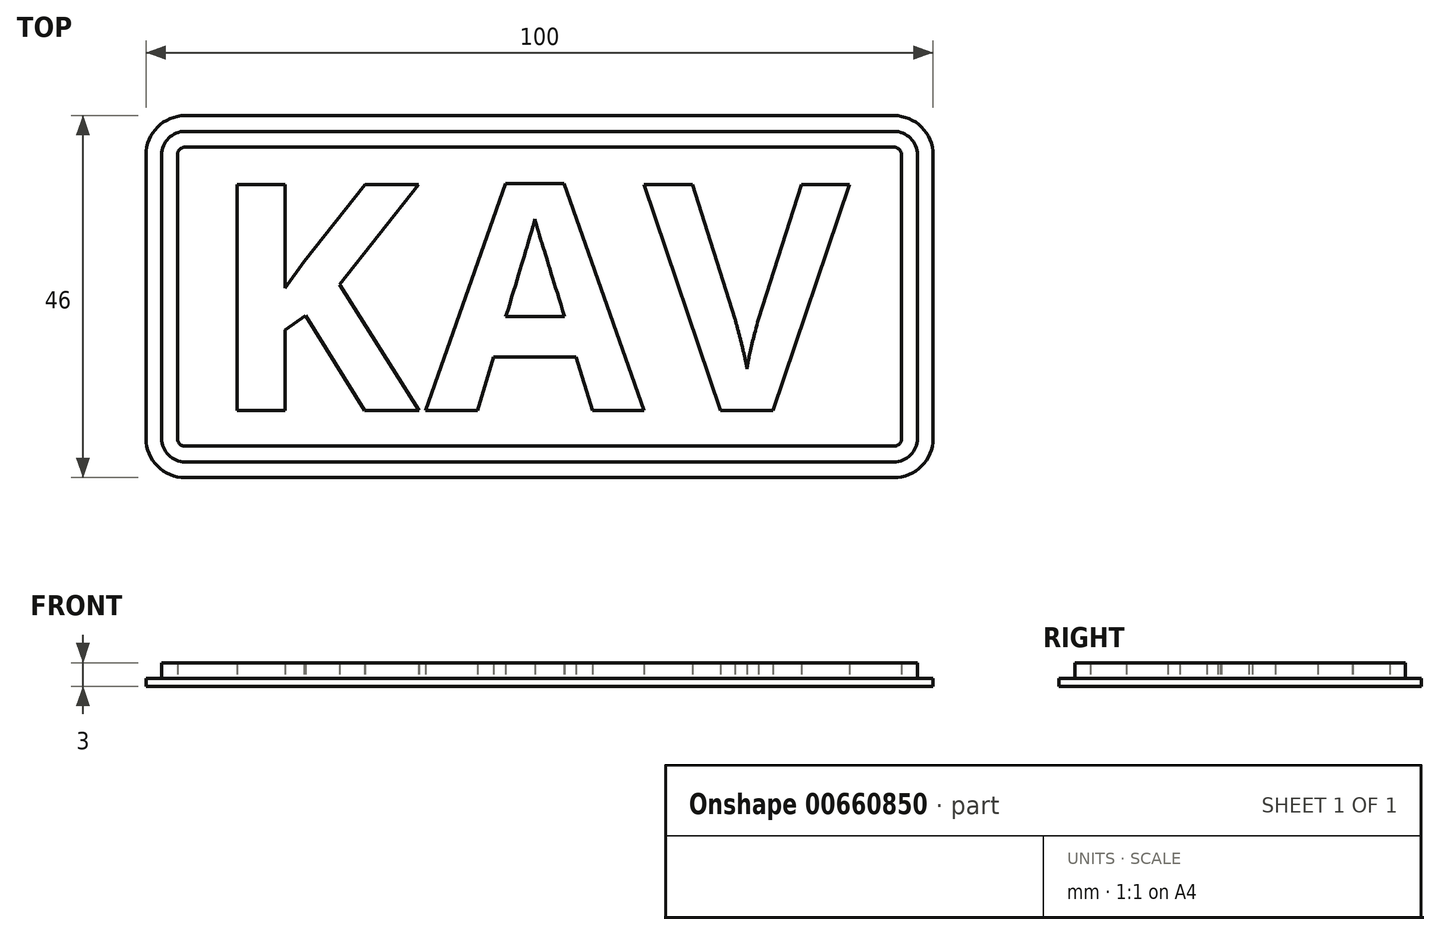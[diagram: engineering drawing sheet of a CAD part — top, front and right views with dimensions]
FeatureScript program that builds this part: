
annotation { "Feature Type Name" : "Feature", "Feature Type Description" : "" }
export const myFeature = defineFeature(function(context is Context, id is Id, definition is map)
    precondition{}
    {
        {
            assignVariable(context, id + "F0", {"variableType" : VariableType.LENGTH, "name" : "st", "lengthValue" : 1 * mm});
        }
        {
            assignVariable(context, id + "F1", {"variableType" : VariableType.LENGTH, "name" : "ft", "lengthValue" : 2 * mm});
        }
        {
            var Q0;
            Q0=qCreatedBy(makeId("Top.planeOp"),FACE);
            var sketch = newSketch(context, id + "F2", { "sketchPlane" : qUnion([Q0])});
            skLineSegment(sketch, "E0.bottom", {"start": v(-45, 23) * mm, "end": v(45, 23) * mm});
            skLineSegment(sketch, "E0.top", {"start": v(-45, -23) * mm, "end": v(45, -23) * mm});
            skLineSegment(sketch, "E0.left", {"start": v(-50, 18) * mm, "end": v(-50, -18) * mm});
            skLineSegment(sketch, "E0.right", {"start": v(50, 18) * mm, "end": v(50, -18) * mm});
            skPoint(sketch, "E1", {"position": v(0, 23) * mm});
            skPoint(sketch, "E2", {"position": v(-50, 0) * mm});
            skPoint(sketch, "E3.visualSharp", {"position": v(-50, 23) * mm});
            skArc(sketch, "E3.filletArc", {"start": v(-45, 23) * mm, "mid": v(-48.54, 21.54) * mm, "end": v(-50, 18) * mm});
            skPoint(sketch, "E4.visualSharp", {"position": v(50, 23) * mm});
            skArc(sketch, "E4.filletArc", {"start": v(50, 18) * mm, "mid": v(48.54, 21.54) * mm, "end": v(45, 23) * mm});
            skPoint(sketch, "E5.visualSharp", {"position": v(50, -23) * mm});
            skArc(sketch, "E5.filletArc", {"start": v(45, -23) * mm, "mid": v(48.54, -21.54) * mm, "end": v(50, -18) * mm});
            skPoint(sketch, "E6.visualSharp", {"position": v(-50, -23) * mm});
            skArc(sketch, "E6.filletArc", {"start": v(-50, -18) * mm, "mid": v(-48.54, -21.54) * mm, "end": v(-45, -23) * mm});
            skSolve(sketch);
        }
        {
            var Q0;
            Q0=qSketchRegion(id+"F2",true);
            extrude(context, id + "F3", {"entities" : qUnion([Q0]), "depth" : getVariable(context, 'st'), "offsetDistance" : 25 * mm});
        }
        {
            var Q0;
            Q0=makeQuery(id+"F3.opExtrude","CAP_FACE",FACE,{"disambiguationData":[OSD([sQuery(id+"F2.wireOp",EDGE,"E0.bottom"),sQuery(id+"F2.wireOp",EDGE,"E0.top"),sQuery(id+"F2.wireOp",EDGE,"E0.left"),sQuery(id+"F2.wireOp",EDGE,"E0.right"),sQuery(id+"F2.wireOp",EDGE,"E3.filletArc"),sQuery(id+"F2.wireOp",EDGE,"E4.filletArc"),sQuery(id+"F2.wireOp",EDGE,"E5.filletArc"),sQuery(id+"F2.wireOp",EDGE,"E6.filletArc")])],"isStart":false});
            var sketch = newSketch(context, id + "F4", { "sketchPlane" : qUnion([Q0])});
            skArc(sketch, "E7.0", {"start": v(-45, 21) * mm, "mid": v(-47.12, 20.12) * mm, "end": v(-48, 18) * mm});
            skLineSegment(sketch, "E7.1", {"start": v(-45, 21) * mm, "end": v(45, 21) * mm});
            skLineSegment(sketch, "E7.2", {"start": v(-48, 18) * mm, "end": v(-48, -18) * mm});
            skArc(sketch, "E7.3", {"start": v(48, 18) * mm, "mid": v(47.12, 20.12) * mm, "end": v(45, 21) * mm});
            skArc(sketch, "E7.4", {"start": v(-48, -18) * mm, "mid": v(-47.12, -20.12) * mm, "end": v(-45, -21) * mm});
            skLineSegment(sketch, "E7.5", {"start": v(-45, -21) * mm, "end": v(45, -21) * mm});
            skArc(sketch, "E7.6", {"start": v(45, -21) * mm, "mid": v(47.12, -20.12) * mm, "end": v(48, -18) * mm});
            skLineSegment(sketch, "E7.7", {"start": v(48, 18) * mm, "end": v(48, -18) * mm});
            skArc(sketch, "E8.0", {"start": v(-45, 19) * mm, "mid": v(-45.7, 18.7) * mm, "end": v(-46, 18) * mm});
            skLineSegment(sketch, "E8.1", {"start": v(-45, 19) * mm, "end": v(45, 19) * mm});
            skLineSegment(sketch, "E8.2", {"start": v(-46, 18) * mm, "end": v(-46, -18) * mm});
            skArc(sketch, "E8.3", {"start": v(46, 18) * mm, "mid": v(45.7, 18.7) * mm, "end": v(45, 19) * mm});
            skArc(sketch, "E8.4", {"start": v(-46, -18) * mm, "mid": v(-45.7, -18.7) * mm, "end": v(-45, -19) * mm});
            skLineSegment(sketch, "E8.5", {"start": v(-45, -19) * mm, "end": v(45, -19) * mm});
            skArc(sketch, "E8.6", {"start": v(45, -19) * mm, "mid": v(45.7, -18.7) * mm, "end": v(46, -18) * mm});
            skLineSegment(sketch, "E8.7", {"start": v(46, 18) * mm, "end": v(46, -18) * mm});
            skText(sketch, "E9", { "text": "KAV", "fontName": "OpenSans-Bold.ttf"});
            const initialGuessF4  = {"E9": [-0.042, -0.01447, 1, 0, 0.02894]};
            skSetInitialGuess(sketch, initialGuessF4);
            skSolve(sketch);
        }
        {
            var Q0;
            Q0=makeQuery(id+"F4.imprint","IMPRINT",FACE,{"disambiguationData":[TD([[makeQuery(id+"F4.imprint","IMPRINT",EDGE,{"derivedFrom":sQuery(id+"F4.wireOp",EDGE,"E9.sketch_text.stroke-0")}),-1.0]])]});
            var Q1;
            Q1=makeQuery(id+"F4.imprint","IMPRINT",FACE,{"disambiguationData":[TD([[makeQuery(id+"F4.imprint","IMPRINT",EDGE,{"derivedFrom":sQuery(id+"F4.wireOp",EDGE,"E9.sketch_text.stroke-13")}),-1.0]])]});
            var Q2;
            Q2=makeQuery(id+"F4.imprint","IMPRINT",FACE,{"disambiguationData":[TD([[makeQuery(id+"F4.imprint","IMPRINT",EDGE,{"derivedFrom":sQuery(id+"F4.wireOp",EDGE,"E9.sketch_text.stroke-26")}),-1.0]])]});
            var Q3;
            Q3=makeQuery(id+"F4.imprint","IMPRINT",FACE,{"disambiguationData":[TD([[makeQuery(id+"F4.imprint","IMPRINT",EDGE,{"derivedFrom":sQuery(id+"F4.wireOp",EDGE,"E7.0")}),1.0]])]});
            extrude(context, id + "F5", {"entities" : qUnion([Q0, Q1, Q2, Q3]), "operationType" : NewBodyOperationType.ADD, "depth" : getVariable(context, 'ft'), "offsetDistance" : 25 * mm});
        }
    });
